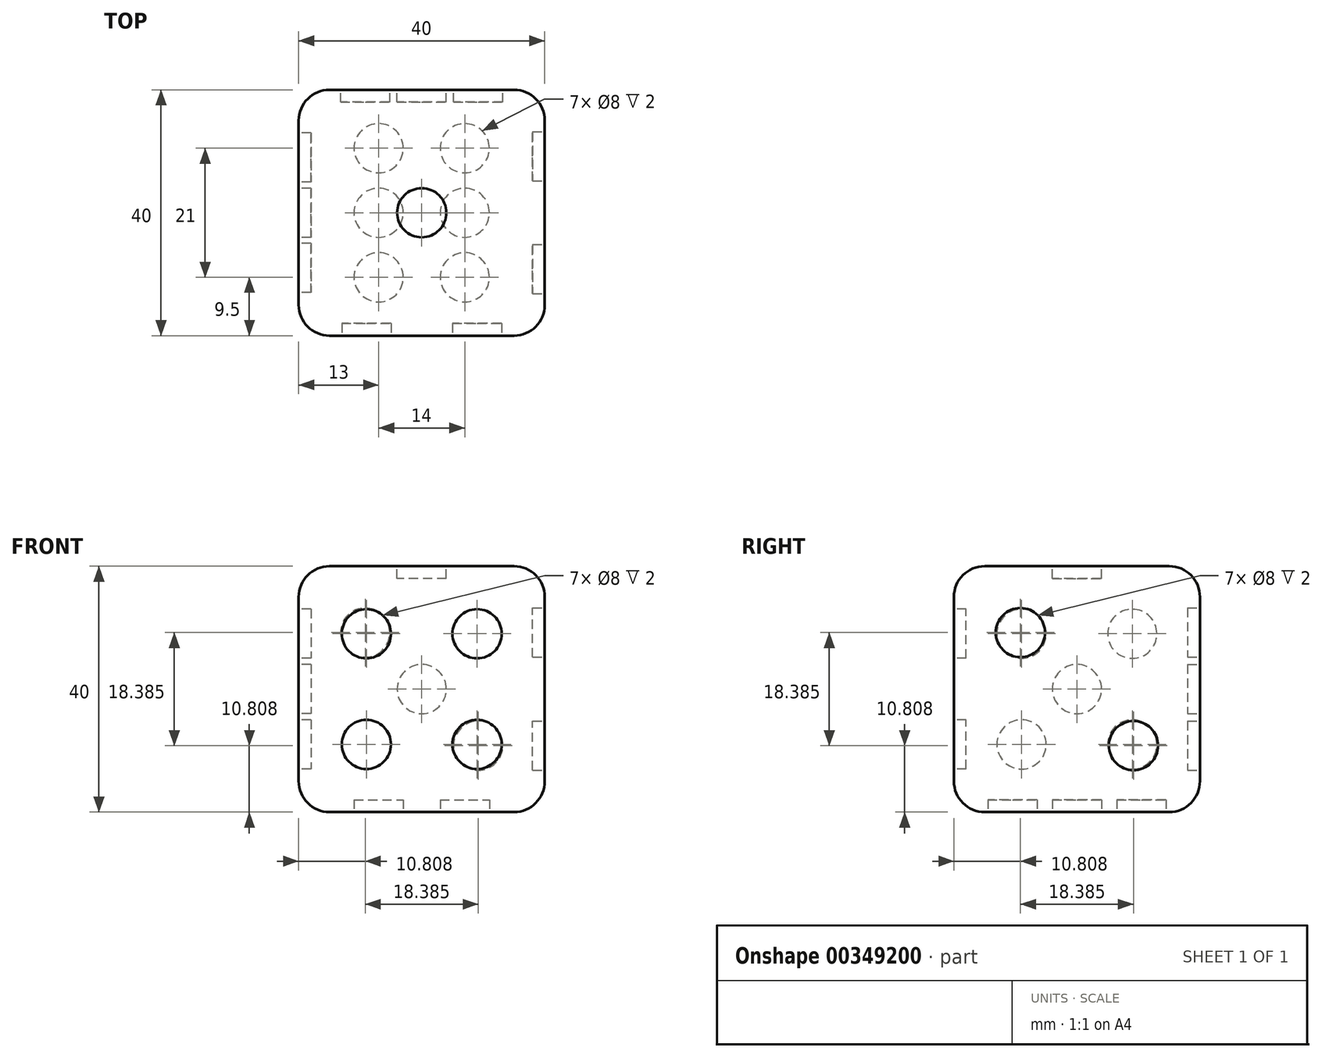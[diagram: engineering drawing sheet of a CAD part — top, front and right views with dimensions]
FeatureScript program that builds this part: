
annotation { "Feature Type Name" : "Feature", "Feature Type Description" : "" }
export const myFeature = defineFeature(function(context is Context, id is Id, definition is map)
    precondition{}
    {
        {
            var Q0;
            Q0=qCreatedBy(makeId("Top.planeOp"),FACE);
            var sketch = newSketch(context, id + "F0", { "sketchPlane" : qUnion([Q0])});
            skLineSegment(sketch, "E0.bottom", {"start": v(0, 0) * mm, "end": v(40, 0) * mm});
            skLineSegment(sketch, "E0.top", {"start": v(0, 40) * mm, "end": v(40, 40) * mm});
            skLineSegment(sketch, "E0.left", {"start": v(0, 0) * mm, "end": v(0, 40) * mm});
            skLineSegment(sketch, "E0.right", {"start": v(40, 0) * mm, "end": v(40, 40) * mm});
            skSolve(sketch);
        }
        {
            var Q0;
            Q0 = qSketchRegion(id + "F0", true);
            extrude(context, id + "F1", {"entities" : qUnion([Q0]), "depth" : 40 * mm});
        }
        {
            var Q0;
            Q0=makeQuery(id+"F1.opExtrude","CAP_FACE",FACE,{"disambiguationData":[OSD([sQuery(id+"F0.wireOp",EDGE,"E0.bottom"),sQuery(id+"F0.wireOp",EDGE,"E0.top"),sQuery(id+"F0.wireOp",EDGE,"E0.left"),sQuery(id+"F0.wireOp",EDGE,"E0.right")])],"isStart":false});
            var sketch = newSketch(context, id + "F2", { "sketchPlane" : qUnion([Q0])});
            skLineSegment(sketch, "E1", {"start": v(0, 20) * mm, "end": v(40, 20) * mm, "construction": true});
            skCircle(sketch, "E2", {"center": v(20, 20) * mm, "radius": 4 * mm});
            skSolve(sketch);
        }
        {
            var Q0;
            Q0 = qSketchRegion(id + "F2", true);
            extrude(context, id + "F3", {"entities" : qUnion([Q0]), "operationType" : NewBodyOperationType.REMOVE, "oppositeDirection" : true, "depth" : 2 * mm});
        }
        {
            var Q0;
            Q0=makeQuery(id+"F1.opExtrude","CAP_FACE",FACE,{"disambiguationData":[OSD([sQuery(id+"F0.wireOp",EDGE,"E0.bottom"),sQuery(id+"F0.wireOp",EDGE,"E0.top"),sQuery(id+"F0.wireOp",EDGE,"E0.left"),sQuery(id+"F0.wireOp",EDGE,"E0.right")])],"isStart":true});
            var sketch = newSketch(context, id + "F4", { "sketchPlane" : qUnion([Q0])});
            skLineSegment(sketch, "E3", {"start": v(0, -20) * mm, "end": v(40, -20) * mm, "construction": true});
            skLineSegment(sketch, "E4", {"start": v(20, 0) * mm, "end": v(20, -40) * mm, "construction": true});
            skCircle(sketch, "E5", {"center": v(13, -20) * mm, "radius": 4 * mm});
            skCircle(sketch, "E6", {"center": v(13, -9.5) * mm, "radius": 4 * mm});
            skCircle(sketch, "E7.MirrorC", {"center": v(13, -30.5) * mm, "radius": 4 * mm});
            skCircle(sketch, "E8.MirrorC", {"center": v(27, -9.5) * mm, "radius": 4 * mm});
            skCircle(sketch, "E9.MirrorC", {"center": v(27, -20) * mm, "radius": 4 * mm});
            skCircle(sketch, "E10.MirrorC", {"center": v(27, -30.5) * mm, "radius": 4 * mm});
            skSolve(sketch);
        }
        {
            var Q0;
            Q0 = qSketchRegion(id + "F4", true);
            extrude(context, id + "F5", {"entities" : qUnion([Q0]), "operationType" : NewBodyOperationType.REMOVE, "oppositeDirection" : true, "depth" : 2 * mm});
        }
        {
            var Q0;
            Q0=makeQuery(id+"F1.opExtrude","SWEPT_FACE",FACE,{"disambiguationData":[OSD([sQuery(id+"F0.wireOp",EDGE,"E0.left")])]});
            var sketch = newSketch(context, id + "F6", { "sketchPlane" : qUnion([Q0])});
            skLineSegment(sketch, "E11", {"start": v(-40, 20) * mm, "end": v(0, 20) * mm, "construction": true});
            skLineSegment(sketch, "E12", {"start": v(-20, 40) * mm, "end": v(-20, 0) * mm, "construction": true});
            skCircle(sketch, "E13", {"center": v(-20, 20) * mm, "radius": 4 * mm});
            skCircle(sketch, "E14", {"center": v(-11, 29) * mm, "radius": 4 * mm});
            skCircle(sketch, "E15.MirrorC", {"center": v(-29, 29) * mm, "radius": 4 * mm});
            skCircle(sketch, "E16.MirrorC", {"center": v(-11, 11) * mm, "radius": 4 * mm});
            skCircle(sketch, "E17.MirrorC", {"center": v(-29, 11) * mm, "radius": 4 * mm});
            skSolve(sketch);
        }
        {
            var Q0;
            Q0 = qSketchRegion(id + "F6", true);
            extrude(context, id + "F7", {"entities" : qUnion([Q0]), "operationType" : NewBodyOperationType.REMOVE, "oppositeDirection" : true, "depth" : 2 * mm});
        }
        {
            var Q0;
            Q0=makeQuery(id+"F1.opExtrude","SWEPT_FACE",FACE,{"disambiguationData":[OSD([sQuery(id+"F0.wireOp",EDGE,"E0.top")])]});
            var sketch = newSketch(context, id + "F8", { "sketchPlane" : qUnion([Q0])});
            skLineSegment(sketch, "E18", {"start": v(-40, 0) * mm, "end": v(0, 40) * mm, "construction": true});
            skCircle(sketch, "E19", {"center": v(-20, 20) * mm, "radius": 4 * mm});
            skCircle(sketch, "E20", {"center": v(-29.2, 10.8) * mm, "radius": 4 * mm});
            skCircle(sketch, "E21", {"center": v(-10.8, 29.2) * mm, "radius": 4 * mm});
            skSolve(sketch);
        }
        {
            var Q0;
            Q0 = qSketchRegion(id + "F8", true);
            extrude(context, id + "F9", {"entities" : qUnion([Q0]), "operationType" : NewBodyOperationType.REMOVE, "oppositeDirection" : true, "depth" : 2 * mm});
        }
        {
            var Q0;
            Q0=makeQuery(id+"F1.opExtrude","SWEPT_FACE",FACE,{"disambiguationData":[OSD([sQuery(id+"F0.wireOp",EDGE,"E0.bottom")])]});
            var sketch = newSketch(context, id + "F10", { "sketchPlane" : qUnion([Q0])});
            skLineSegment(sketch, "E22", {"start": v(0, 20) * mm, "end": v(40, 20) * mm, "construction": true});
            skLineSegment(sketch, "E23", {"start": v(20, 40) * mm, "end": v(20, 0) * mm, "construction": true});
            skCircle(sketch, "E24", {"center": v(29, 29) * mm, "radius": 4 * mm});
            skCircle(sketch, "E25.MirrorC", {"center": v(11, 29) * mm, "radius": 4 * mm});
            skCircle(sketch, "E26.MirrorC", {"center": v(11, 11) * mm, "radius": 4 * mm});
            skCircle(sketch, "E27.MirrorC", {"center": v(29, 11) * mm, "radius": 4 * mm});
            skSolve(sketch);
        }
        {
            var Q0;
            Q0 = qSketchRegion(id + "F10", true);
            extrude(context, id + "F11", {"entities" : qUnion([Q0]), "operationType" : NewBodyOperationType.REMOVE, "oppositeDirection" : true, "depth" : 2 * mm});
        }
        {
            var Q0;
            Q0=makeQuery(id+"F1.opExtrude","SWEPT_FACE",FACE,{"disambiguationData":[OSD([sQuery(id+"F0.wireOp",EDGE,"E0.right")])]});
            var sketch = newSketch(context, id + "F12", { "sketchPlane" : qUnion([Q0])});
            skLineSegment(sketch, "E28", {"start": v(0, 40) * mm, "end": v(40, 0) * mm, "construction": true});
            skCircle(sketch, "E29", {"center": v(10.8, 29.2) * mm, "radius": 4 * mm});
            skCircle(sketch, "E30", {"center": v(29.2, 10.8) * mm, "radius": 4 * mm});
            skLineSegment(sketch, "E31", {"start": v(0, 0) * mm, "end": v(40, 40) * mm, "construction": true});
            skSolve(sketch);
        }
        {
            var Q0;
            Q0 = qSketchRegion(id + "F12", true);
            extrude(context, id + "F13", {"entities" : qUnion([Q0]), "operationType" : NewBodyOperationType.REMOVE, "oppositeDirection" : true, "depth" : 2 * mm});
        }
        {
            var Q0;
            Q0=makeQuery(id+"F1.opExtrude","CAP_EDGE",EDGE,{"disambiguationData":[OSD([sQuery(id+"F0.wireOp",EDGE,"E0.top")])],"isStart":false});
            var Q1;
            Q1=makeQuery(id+"F1.opExtrude","SWEPT_EDGE",EDGE,{"disambiguationData":[OSD([sQuery(id+"F0.wireOp",EDGE,"E0.top"),sQuery(id+"F0.wireOp",EDGE,"E0.right")])]});
            var Q2;
            Q2=makeQuery(id+"F1.opExtrude","CAP_EDGE",EDGE,{"disambiguationData":[OSD([sQuery(id+"F0.wireOp",EDGE,"E0.right")])],"isStart":false});
            var Q3;
            Q3=makeQuery(id+"F1.opExtrude","CAP_EDGE",EDGE,{"disambiguationData":[OSD([sQuery(id+"F0.wireOp",EDGE,"E0.right")])],"isStart":true});
            var Q4;
            Q4=makeQuery(id+"F1.opExtrude","SWEPT_EDGE",EDGE,{"disambiguationData":[OSD([sQuery(id+"F0.wireOp",EDGE,"E0.bottom"),sQuery(id+"F0.wireOp",EDGE,"E0.right")])]});
            var Q5;
            Q5=makeQuery(id+"F1.opExtrude","CAP_EDGE",EDGE,{"disambiguationData":[OSD([sQuery(id+"F0.wireOp",EDGE,"E0.bottom")])],"isStart":false});
            var Q6;
            Q6=makeQuery(id+"F1.opExtrude","CAP_EDGE",EDGE,{"disambiguationData":[OSD([sQuery(id+"F0.wireOp",EDGE,"E0.left")])],"isStart":false});
            var Q7;
            Q7=makeQuery(id+"F1.opExtrude","SWEPT_EDGE",EDGE,{"disambiguationData":[OSD([sQuery(id+"F0.wireOp",EDGE,"E0.bottom"),sQuery(id+"F0.wireOp",EDGE,"E0.left")])]});
            var Q8;
            Q8=makeQuery(id+"F1.opExtrude","SWEPT_EDGE",EDGE,{"disambiguationData":[OSD([sQuery(id+"F0.wireOp",EDGE,"E0.top"),sQuery(id+"F0.wireOp",EDGE,"E0.left")])]});
            var Q9;
            Q9=makeQuery(id+"F1.opExtrude","CAP_EDGE",EDGE,{"disambiguationData":[OSD([sQuery(id+"F0.wireOp",EDGE,"E0.top")])],"isStart":true});
            var Q10;
            Q10=makeQuery(id+"F1.opExtrude","CAP_EDGE",EDGE,{"disambiguationData":[OSD([sQuery(id+"F0.wireOp",EDGE,"E0.left")])],"isStart":true});
            var Q11;
            Q11=makeQuery(id+"F1.opExtrude","CAP_EDGE",EDGE,{"disambiguationData":[OSD([sQuery(id+"F0.wireOp",EDGE,"E0.bottom")])],"isStart":true});
            fillet(context, id + "F14", {"entities" : qUnion([Q0, Q1, Q2, Q3, Q4, Q5, Q6, Q7, Q8, Q9, Q10, Q11]), "radius" : 5 * mm, "tangentPropagation" : true, "allowEdgeOverflow" : false});
        }
    });
